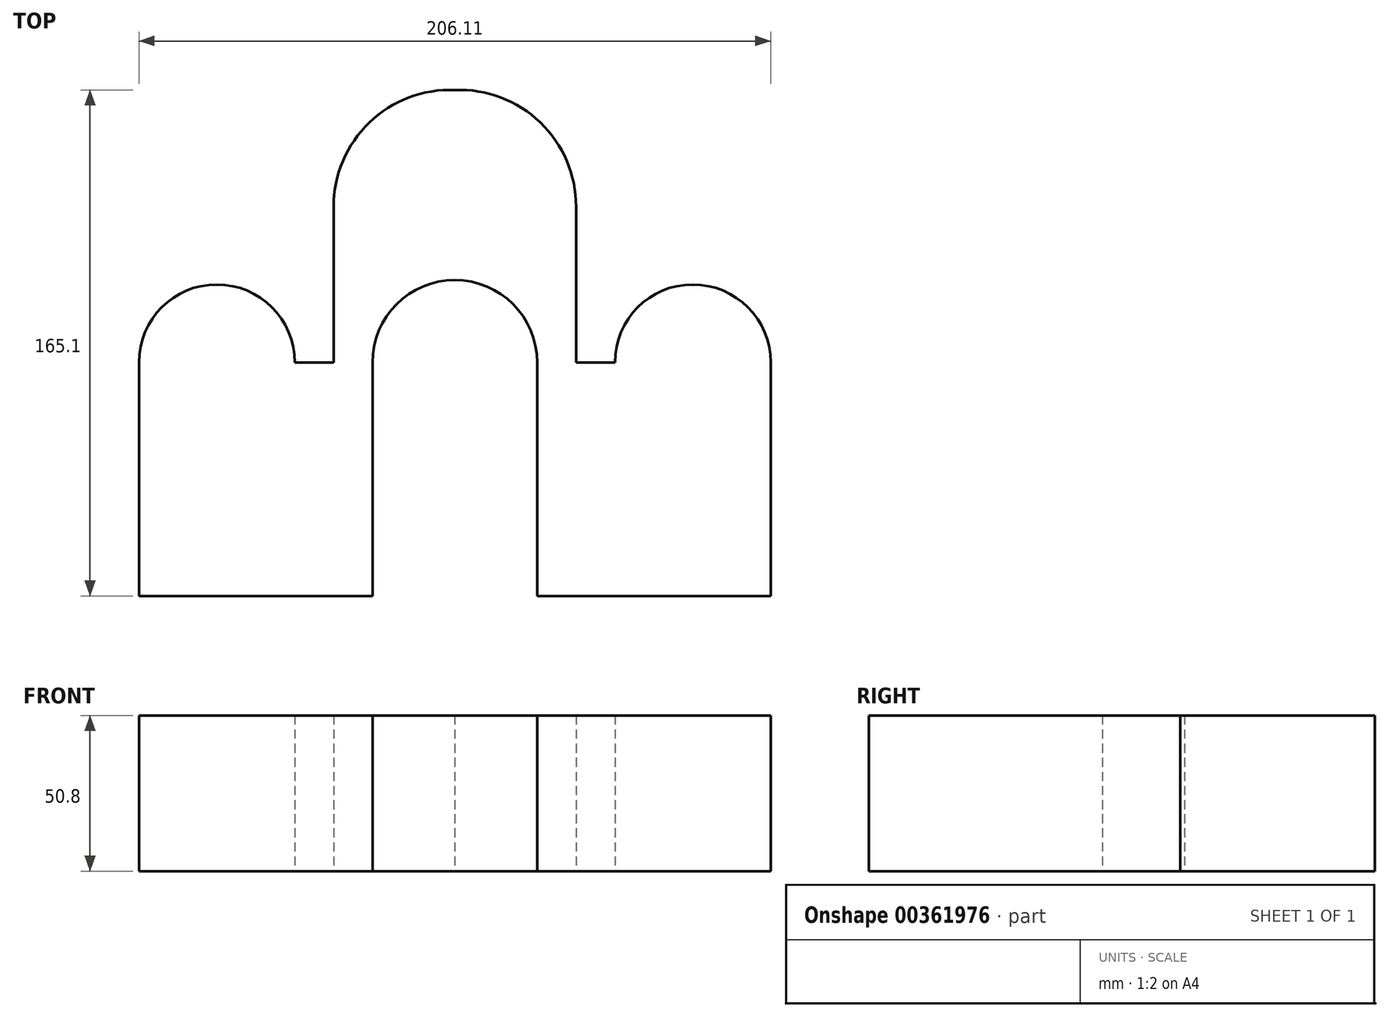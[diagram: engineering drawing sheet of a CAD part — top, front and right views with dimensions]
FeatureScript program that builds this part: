
annotation { "Feature Type Name" : "Feature", "Feature Type Description" : "" }
export const myFeature = defineFeature(function(context is Context, id is Id, definition is map)
    precondition{}
    {
        {
            var Q0;
            Q0=qCreatedBy(makeId("Top.planeOp"),FACE);
            var sketch = newSketch(context, id + "F0", { "sketchPlane" : qUnion([Q0])});
            skLineSegment(sketch, "E0", {"start": v(0, 0) * mm, "end": v(76.2, 0) * mm});
            skLineSegment(sketch, "E1", {"start": v(0, 0) * mm, "end": v(0, 76.2) * mm});
            skLineSegment(sketch, "E2", {"start": v(76.2, 0) * mm, "end": v(76.2, 76.2) * mm});
            skArc(sketch, "E3", {"start": v(0, 76.2) * mm, "mid": v(25.4, 101.6) * mm, "end": v(50.8, 76.2) * mm});
            skLineSegment(sketch, "E4", {"start": v(0, 76.2) * mm, "end": v(50.8, 76.2) * mm});
            skArc(sketch, "E5", {"start": v(76.2, 76.2) * mm, "mid": v(84.06, 95.19) * mm, "end": v(103.05, 103.05) * mm});
            skLineSegment(sketch, "E6", {"start": v(50.8, 76.2) * mm, "end": v(63.5, 76.2) * mm});
            skLineSegment(sketch, "E7", {"start": v(63.5, 76.2) * mm, "end": v(63.5, 127) * mm});
            skArc(sketch, "E8", {"start": v(63.5, 127) * mm, "mid": v(75.18, 154.45) * mm, "end": v(103.05, 165.07) * mm});
            skLineSegment(sketch, "E9", {"start": v(103.05, 76.2) * mm, "end": v(103.05, 103.05) * mm, "construction": true});
            skArc(sketch, "E10.MirrorCS", {"start": v(129.9, 76.2) * mm, "mid": v(122.04, 95.19) * mm, "end": v(103.05, 103.05) * mm});
            skLineSegment(sketch, "E11", {"start": v(103.05, 165.07) * mm, "end": v(103.05, 103.05) * mm, "construction": true});
            skArc(sketch, "E12.MirrorCS", {"start": v(142.6, 127) * mm, "mid": v(130.93, 154.45) * mm, "end": v(103.05, 165.07) * mm});
            skLineSegment(sketch, "E13.MirrorCS", {"start": v(142.6, 76.2) * mm, "end": v(142.6, 127) * mm});
            skLineSegment(sketch, "E14.MirrorCS", {"start": v(155.3, 76.2) * mm, "end": v(142.6, 76.2) * mm});
            skArc(sketch, "E15.MirrorCS", {"start": v(206.1, 76.2) * mm, "mid": v(180.7, 101.6) * mm, "end": v(155.3, 76.2) * mm});
            skLineSegment(sketch, "E16.MirrorCS", {"start": v(206.1, 0) * mm, "end": v(206.1, 76.2) * mm});
            skLineSegment(sketch, "E17.MirrorCS", {"start": v(206.1, 0) * mm, "end": v(129.9, 0) * mm});
            skLineSegment(sketch, "E18.MirrorCS", {"start": v(129.9, 0) * mm, "end": v(129.9, 76.2) * mm});
            skSolve(sketch);
        }
        {
            var Q0;
            Q0 = qSketchRegion(id + "F0", true);
            extrude(context, id + "F1", {"entities" : qUnion([Q0]), "depth" : 50.8 * mm});
        }
    });
